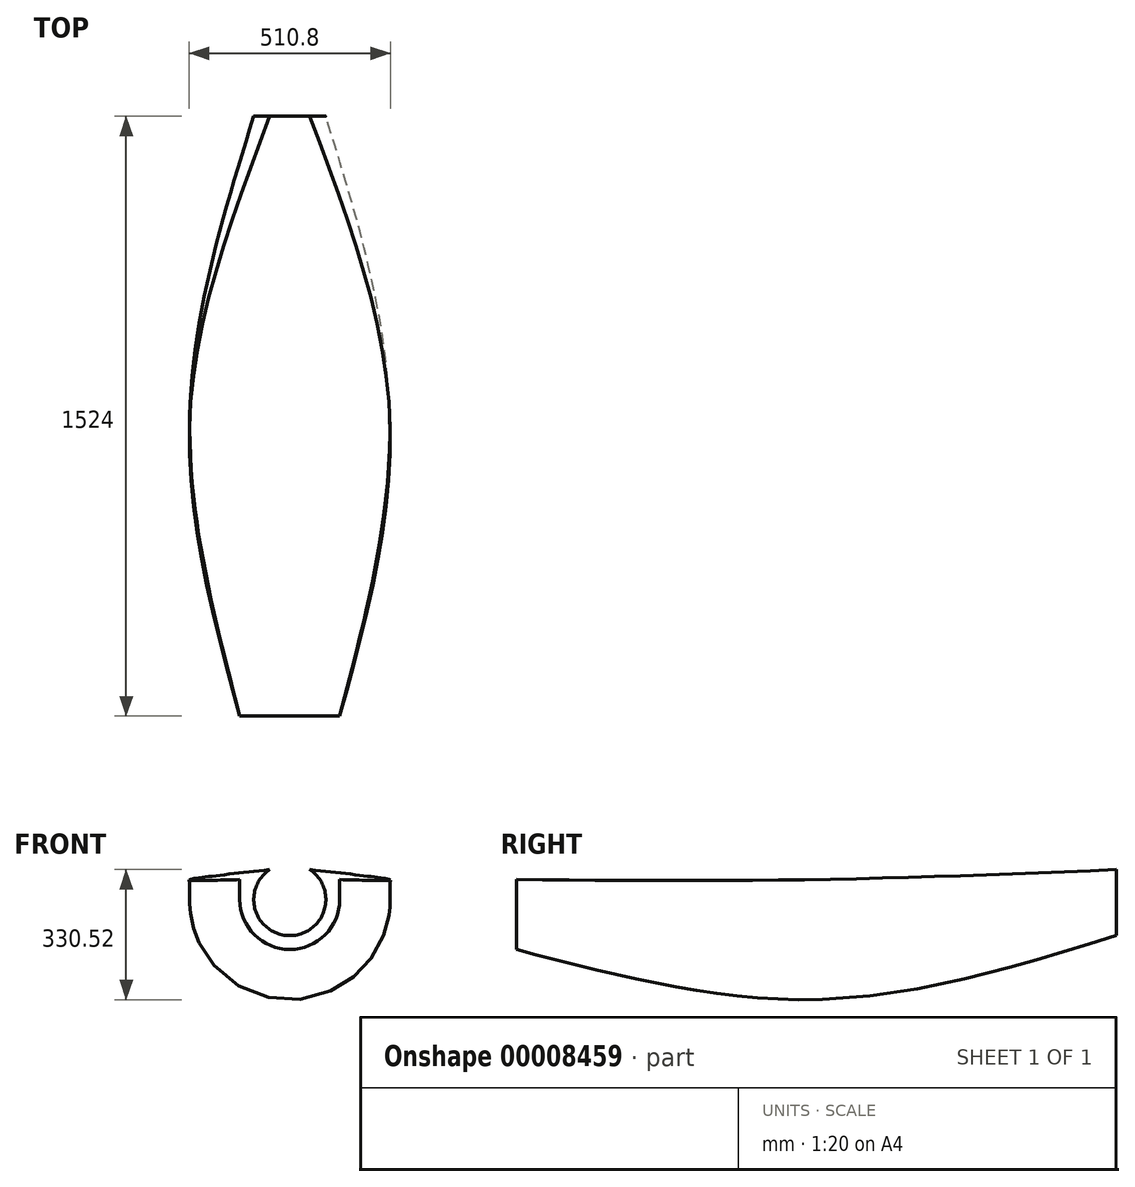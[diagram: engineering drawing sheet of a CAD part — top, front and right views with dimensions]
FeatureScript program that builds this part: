
annotation { "Feature Type Name" : "Feature", "Feature Type Description" : "" }
export const myFeature = defineFeature(function(context is Context, id is Id, definition is map)
    precondition{}
    {
        {
            var Q0;
            Q0=qCreatedBy(makeId("Front.planeOp"),FACE);
            cPlane(context, id + "F0", {"entities" : qUnion([Q0]), "cplaneType" : CPlaneType.OFFSET, "offset" : 762 * mm, "width" : 152.4 * mm, "height" : 152.4 * mm});
        }
        {
            var Q0;
            Q0=qCreatedBy(id+"F0.planeOp",FACE);
            cPlane(context, id + "F1", {"entities" : qUnion([Q0]), "cplaneType" : CPlaneType.OFFSET, "offset" : 762 * mm, "width" : 152.4 * mm, "height" : 152.4 * mm});
        }
        {
            var Q0;
            Q0=qCreatedBy(id+"F1.planeOp",FACE);
            var sketch = newSketch(context, id + "F2", { "sketchPlane" : qUnion([Q0])});
            skLineSegment(sketch, "E0", {"start": v(-127, 50.8) * mm, "end": v(-127, 0) * mm});
            skArc(sketch, "E1", {"start": v(-127, 0) * mm, "mid": v(0, -127) * mm, "end": v(127, 0) * mm});
            skLineSegment(sketch, "E2", {"start": v(127, 0) * mm, "end": v(127, 50.8) * mm});
            skSolve(sketch);
        }
        {
            var Q0;
            Q0=qCreatedBy(id+"F0.planeOp",FACE);
            var sketch = newSketch(context, id + "F3", { "sketchPlane" : qUnion([Q0])});
            skArc(sketch, "E3", {"start": v(-254, 0) * mm, "mid": v(0, -254) * mm, "end": v(254, 0) * mm});
            skLineSegment(sketch, "E4", {"start": v(-254, 0) * mm, "end": v(-254, 50.8) * mm});
            skLineSegment(sketch, "E5", {"start": v(254, 0) * mm, "end": v(254, 50.8) * mm});
            skSolve(sketch);
        }
        {
            var Q0;
            Q0=qCreatedBy(makeId("Front.planeOp"),FACE);
            var sketch = newSketch(context, id + "F4", { "sketchPlane" : qUnion([Q0])});
            skArc(sketch, "E6", {"start": v(-50.8, 76.2) * mm, "mid": v(0, -91.58) * mm, "end": v(50.8, 76.2) * mm});
            skSolve(sketch);
        }
        {
            var Q0;
            Q0 = qSketchRegion(id + "F2", true);
            var Q1;
            Q1 = qSketchRegion(id + "F3", true);
            var Q2;
            Q2 = qBodyType(qCreatedBy(id + "F2" ,EDGE), BodyType.WIRE);
            var Q3;
            Q3 = qBodyType(qCreatedBy(id + "F3" ,EDGE), BodyType.WIRE);
            var Q4;
            Q4 = qBodyType(qCreatedBy(id + "F4" ,EDGE), BodyType.WIRE);
            loft(context, id + "F5", {"bodyType" : ToolBodyType.SURFACE, "sheetProfilesArray" : [{ "sheetProfileEntities" : qUnion([Q0]) }, { "sheetProfileEntities" : qUnion([Q1]) }], "wireProfilesArray" : [{ "wireProfileEntities" : qUnion([Q2]) }, { "wireProfileEntities" : qUnion([Q3]) }, { "wireProfileEntities" : qUnion([Q4]) }]});
        }
    });
